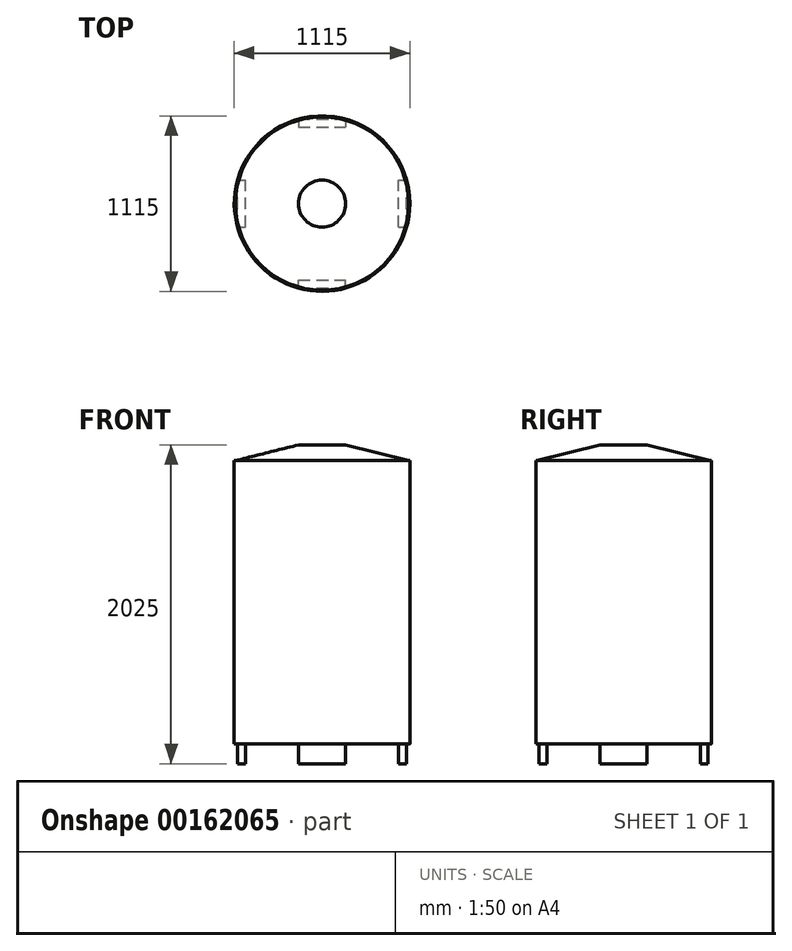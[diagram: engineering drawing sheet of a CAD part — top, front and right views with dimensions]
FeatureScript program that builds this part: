
annotation { "Feature Type Name" : "Feature", "Feature Type Description" : "" }
export const myFeature = defineFeature(function(context is Context, id is Id, definition is map)
    precondition{}
    {
        {
            var Q0;
            Q0=qCreatedBy(makeId("Top.planeOp"),FACE);
            var sketch = newSketch(context, id + "F0", { "sketchPlane" : qUnion([Q0])});
            skCircle(sketch, "E0", {"center": v(0, 0) * mm, "radius": 557.5 * mm});
            skSolve(sketch);
        }
        {
            var Q0;
            Q0 = qSketchRegion(id + "F0", true);
            extrude(context, id + "F1", {"entities" : qUnion([Q0]), "depth" : 1800 * mm});
        }
        {
            var Q0;
            Q0=makeQuery(id+"F1.opExtrude","CAP_FACE",FACE,{"disambiguationData":[OSD([sQuery(id+"F0.wireOp",EDGE,"E0")])],"isStart":true});
            var sketch = newSketch(context, id + "F2", { "sketchPlane" : qUnion([Q0])});
            skLineSegment(sketch, "E1.bottom", {"start": v(-150, 536.94) * mm, "end": v(150, 536.94) * mm});
            skLineSegment(sketch, "E1.top", {"start": v(-150, 486.94) * mm, "end": v(150, 486.94) * mm});
            skLineSegment(sketch, "E1.left", {"start": v(-150, 536.94) * mm, "end": v(-150, 486.94) * mm});
            skLineSegment(sketch, "E1.right", {"start": v(150, 536.94) * mm, "end": v(150, 486.94) * mm});
            skLineSegment(sketch, "E2.bottom", {"start": v(-150, -536.94) * mm, "end": v(150, -536.94) * mm});
            skLineSegment(sketch, "E2.top", {"start": v(-150, -486.94) * mm, "end": v(150, -486.94) * mm});
            skLineSegment(sketch, "E2.left", {"start": v(-150, -536.94) * mm, "end": v(-150, -486.94) * mm});
            skLineSegment(sketch, "E2.right", {"start": v(150, -536.94) * mm, "end": v(150, -486.94) * mm});
            skLineSegment(sketch, "E3.bottom", {"start": v(-536.94, 150) * mm, "end": v(-486.94, 150) * mm});
            skLineSegment(sketch, "E3.top", {"start": v(-536.94, -150) * mm, "end": v(-486.94, -150) * mm});
            skLineSegment(sketch, "E3.left", {"start": v(-536.94, 150) * mm, "end": v(-536.94, -150) * mm});
            skLineSegment(sketch, "E3.right", {"start": v(-486.94, 150) * mm, "end": v(-486.94, -150) * mm});
            skLineSegment(sketch, "E4.bottom", {"start": v(486.94, 150) * mm, "end": v(536.94, 150) * mm});
            skLineSegment(sketch, "E4.top", {"start": v(486.94, -150) * mm, "end": v(536.94, -150) * mm});
            skLineSegment(sketch, "E4.left", {"start": v(486.94, 150) * mm, "end": v(486.94, -150) * mm});
            skLineSegment(sketch, "E4.right", {"start": v(536.94, 150) * mm, "end": v(536.94, -150) * mm});
            skSolve(sketch);
        }
        {
            var Q0;
            Q0 = qSketchRegion(id + "F2", true);
            extrude(context, id + "F3", {"entities" : qUnion([Q0]), "operationType" : NewBodyOperationType.ADD, "depth" : 125 * mm});
        }
        {
            var Q0;
            Q0=qCreatedBy(makeId("Right.planeOp"),FACE);
            var sketch = newSketch(context, id + "F4", { "sketchPlane" : qUnion([Q0])});
            skLineSegment(sketch, "E5", {"start": v(0, 1800) * mm, "end": v(0, 1900) * mm});
            skLineSegment(sketch, "E6", {"start": v(-550, 1800) * mm, "end": v(0, 1800) * mm});
            skLineSegment(sketch, "E7", {"start": v(0, 1900) * mm, "end": v(-150, 1900) * mm});
            skLineSegment(sketch, "E8", {"start": v(-150, 1900) * mm, "end": v(-550, 1800) * mm});
            skSolve(sketch);
        }
        {
            var Q0;
            Q0=makeQuery(id+"F4.imprint","IMPRINT",FACE,{"disambiguationData":[TD([[makeQuery(id+"F4.imprint","IMPRINT",EDGE,{"derivedFrom":sQuery(id+"F4.wireOp",EDGE,"E5")}),1.0]])]});
            var Q1;
            Q1=sQuery(id+"F4.wireOp",EDGE,"E5");
            revolve(context, id + "F5", {"entities" : qUnion([Q0]), "axis" : qUnion([Q1]), "revolveType" : RevolveType.FULL});
        }
    });
